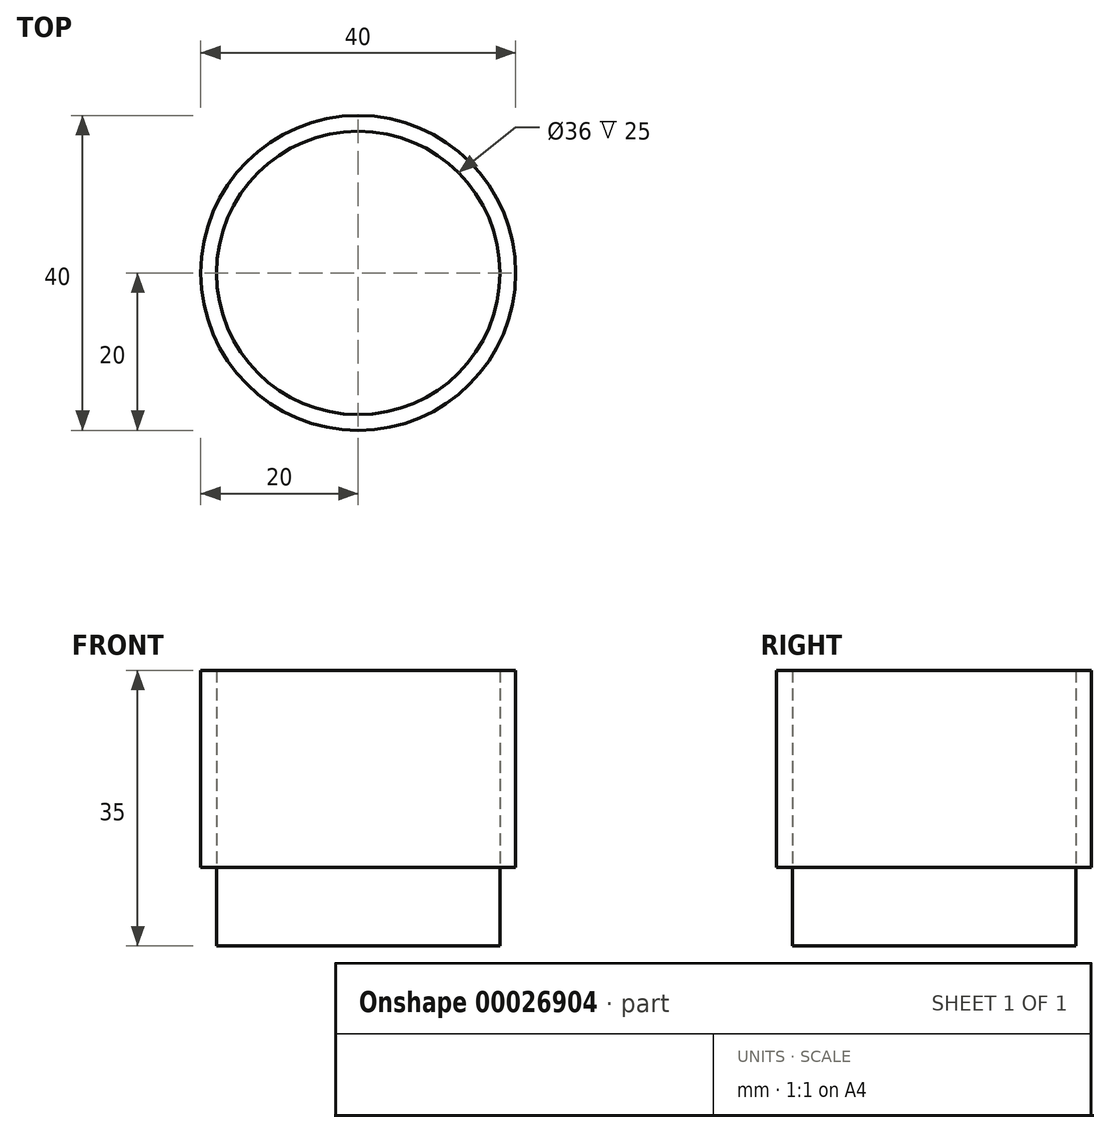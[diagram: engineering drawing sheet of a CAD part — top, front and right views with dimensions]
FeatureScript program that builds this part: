
annotation { "Feature Type Name" : "Feature", "Feature Type Description" : "" }
export const myFeature = defineFeature(function(context is Context, id is Id, definition is map)
    precondition{}
    {
        {
            var Q0;
            Q0=qCreatedBy(makeId("Top.planeOp"),FACE);
            var sketch = newSketch(context, id + "F0", { "sketchPlane" : qUnion([Q0])});
            skCircle(sketch, "E0", {"center": v(0, 0) * mm, "radius": 20 * mm});
            skCircle(sketch, "E1", {"center": v(0, 0) * mm, "radius": 18 * mm});
            skSolve(sketch);
        }
        {
            var Q0;
            Q0=makeQuery(id+"F0.imprint","IMPRINT",FACE,{"disambiguationData":[TD([[makeQuery(id+"F0.imprint","IMPRINT",EDGE,{"derivedFrom":sQuery(id+"F0.wireOp",EDGE,"E1")}),1.0]])]});
            extrude(context, id + "F1", {"entities" : qUnion([Q0]), "oppositeDirection" : true, "depth" : 10 * mm});
        }
        {
            var Q0;
            Q0=makeQuery(id+"F0.imprint","IMPRINT",FACE,{"disambiguationData":[TD([[makeQuery(id+"F0.imprint","IMPRINT",EDGE,{"derivedFrom":sQuery(id+"F0.wireOp",EDGE,"E0")}),1.0]])]});
            extrude(context, id + "F2", {"entities" : qUnion([Q0]), "depth" : 25 * mm});
        }
    });
